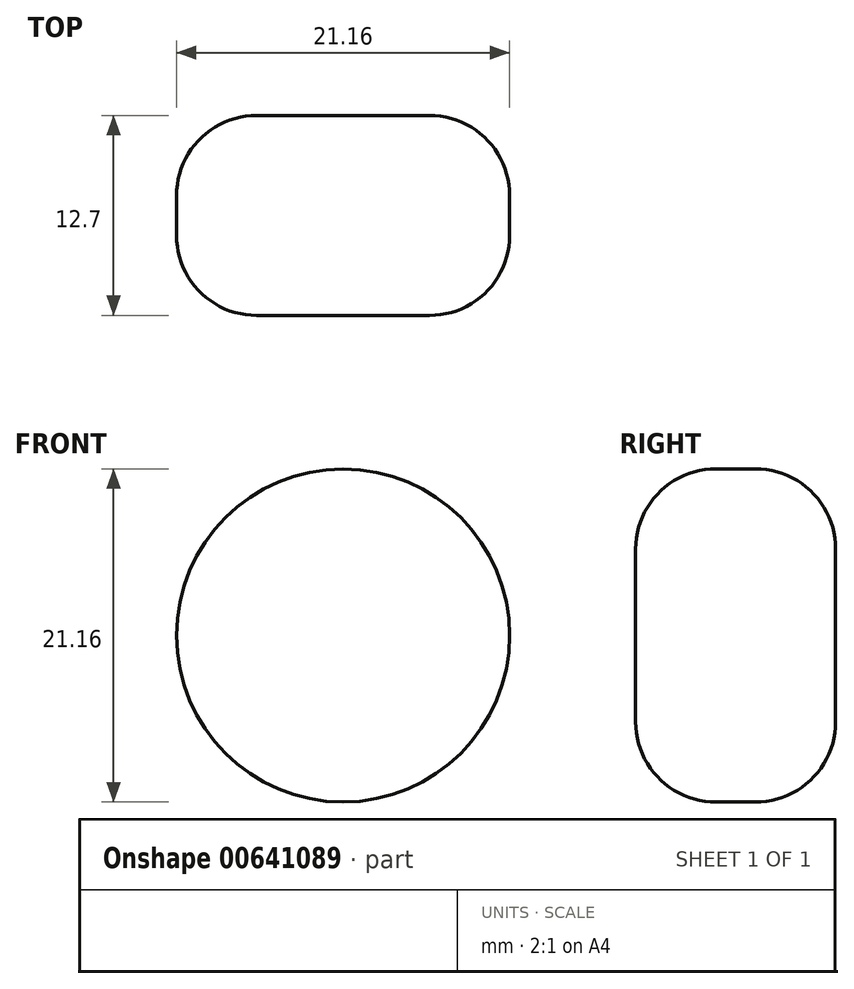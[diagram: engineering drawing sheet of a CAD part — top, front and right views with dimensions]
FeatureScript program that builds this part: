
annotation { "Feature Type Name" : "Feature", "Feature Type Description" : "" }
export const myFeature = defineFeature(function(context is Context, id is Id, definition is map)
    precondition{}
    {
        {
            var Q0;
            Q0=qCreatedBy(makeId("Front.planeOp"),FACE);
            var sketch = newSketch(context, id + "F0", { "sketchPlane" : qUnion([Q0])});
            skCircle(sketch, "E0", {"center": v(0, 0) * mm, "radius": 10.58 * mm});
            skSolve(sketch);
        }
        {
            var Q0;
            Q0 = qSketchRegion(id + "F0", true);
            extrude(context, id + "F1", {"entities" : qUnion([Q0]), "depth" : 12.7 * mm, "offsetDistance" : 25.4 * mm});
        }
        {
            var Q0;
            Q0=makeQuery(id+"F1.opExtrude","CAP_FACE",FACE,{"disambiguationData":[OSD([sQuery(id+"F0.wireOp",EDGE,"E0")])],"isStart":false});
            fillet(context, id + "F2", {"entities" : qUnion([Q0]), "radius" : 5.08 * mm, "tangentPropagation" : true, "allowEdgeOverflow" : false});
        }
        {
            var Q0;
            Q0=makeQuery(id+"F1.opExtrude","CAP_FACE",FACE,{"disambiguationData":[OSD([sQuery(id+"F0.wireOp",EDGE,"E0")])],"isStart":true});
            fillet(context, id + "F3", {"entities" : qUnion([Q0]), "radius" : 5.08 * mm, "tangentPropagation" : true, "allowEdgeOverflow" : false});
        }
    });
